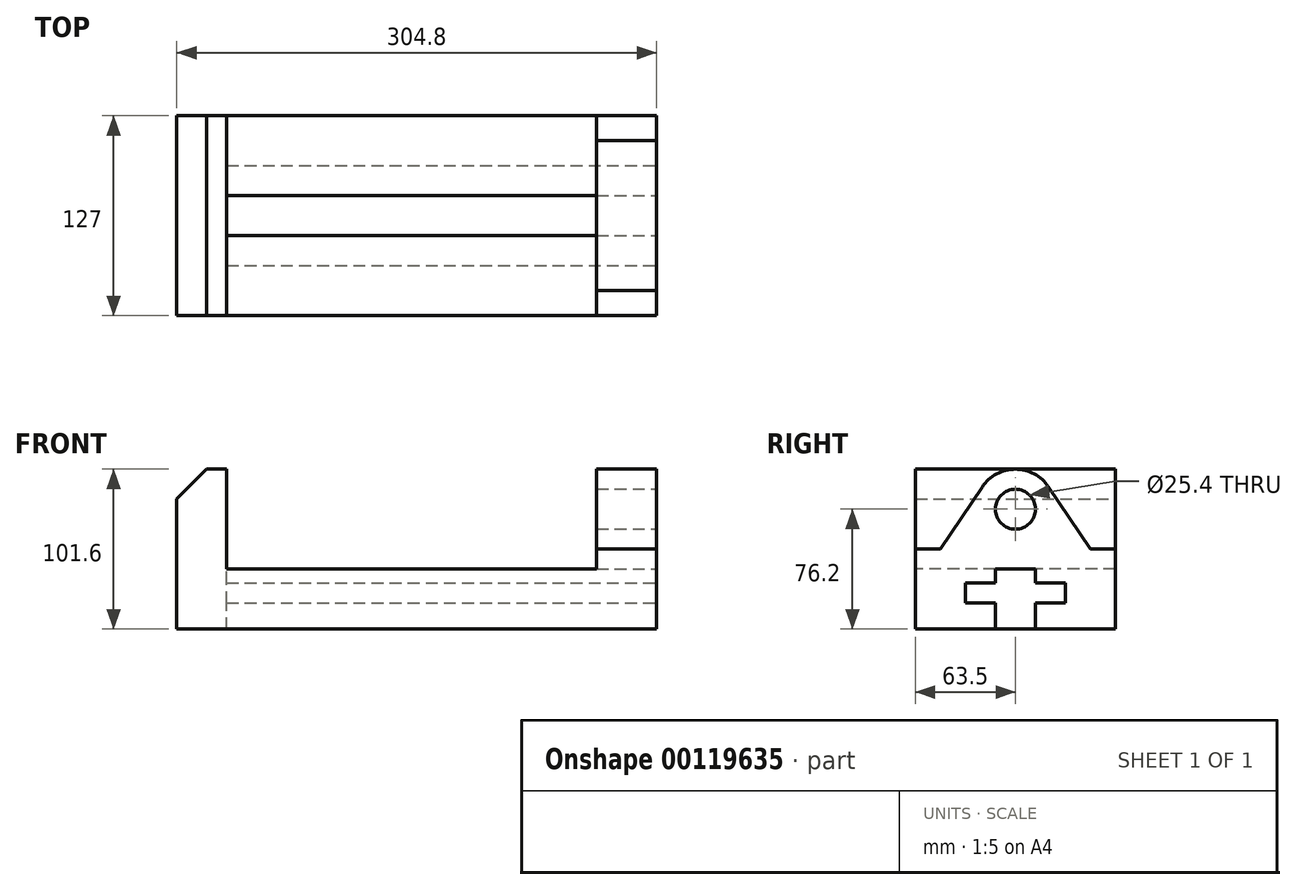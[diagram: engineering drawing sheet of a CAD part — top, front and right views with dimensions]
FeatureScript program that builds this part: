
annotation { "Feature Type Name" : "Feature", "Feature Type Description" : "" }
export const myFeature = defineFeature(function(context is Context, id is Id, definition is map)
    precondition{}
    {
        {
            var Q0;
            Q0=qCreatedBy(makeId("Front.planeOp"),FACE);
            var sketch = newSketch(context, id + "F0", { "sketchPlane" : qUnion([Q0])});
            skLineSegment(sketch, "E0", {"start": v(0, 0) * mm, "end": v(-304.8, 0) * mm});
            skLineSegment(sketch, "E1", {"start": v(-304.8, 0) * mm, "end": v(-304.8, 101.6) * mm});
            skLineSegment(sketch, "E2", {"start": v(-304.8, 101.6) * mm, "end": v(-273.05, 101.6) * mm});
            skLineSegment(sketch, "E3", {"start": v(-273.05, 101.6) * mm, "end": v(-273.05, 38.1) * mm});
            skLineSegment(sketch, "E4", {"start": v(-273.05, 38.1) * mm, "end": v(-38.1, 38.1) * mm});
            skLineSegment(sketch, "E5", {"start": v(-38.1, 38.1) * mm, "end": v(-38.1, 101.6) * mm});
            skLineSegment(sketch, "E6", {"start": v(-38.1, 101.6) * mm, "end": v(0, 101.6) * mm});
            skLineSegment(sketch, "E7", {"start": v(0, 101.6) * mm, "end": v(0, 0) * mm});
            skSolve(sketch);
        }
        {
            var Q0;
            Q0 = qSketchRegion(id + "F0", true);
            extrude(context, id + "F1", {"entities" : qUnion([Q0]), "oppositeDirection" : true, "depth" : 127 * mm});
        }
        {
            var Q0;
            Q0=makeQuery(id+"F1.opExtrude","SWEPT_EDGE",EDGE,{"disambiguationData":[OSD([sQuery(id+"F0.wireOp",EDGE,"E1"),sQuery(id+"F0.wireOp",EDGE,"E2")])]});
            chamfer(context, id + "F2", {"entities" : qUnion([Q0]), "width" : 19.05 * mm, "tangentPropagation" : true});
        }
        {
            var Q0;
            Q0=makeQuery(id+"F1.opExtrude","SWEPT_FACE",FACE,{"disambiguationData":[OSD([sQuery(id+"F0.wireOp",EDGE,"E7")])]});
            var sketch = newSketch(context, id + "F3", { "sketchPlane" : qUnion([Q0])});
            skLineSegment(sketch, "E8", {"start": v(63.5, 0) * mm, "end": v(50.8, 0) * mm});
            skLineSegment(sketch, "E9", {"start": v(50.8, 0) * mm, "end": v(50.8, 16.51) * mm});
            skLineSegment(sketch, "E10", {"start": v(50.8, 16.51) * mm, "end": v(31.75, 16.51) * mm});
            skLineSegment(sketch, "E11", {"start": v(31.75, 16.51) * mm, "end": v(31.75, 29.21) * mm});
            skLineSegment(sketch, "E12", {"start": v(31.75, 29.21) * mm, "end": v(50.8, 29.21) * mm});
            skLineSegment(sketch, "E13", {"start": v(50.8, 29.21) * mm, "end": v(50.8, 38.1) * mm});
            skLineSegment(sketch, "E14", {"start": v(50.8, 38.1) * mm, "end": v(76.2, 38.1) * mm});
            skLineSegment(sketch, "E15", {"start": v(76.2, 38.1) * mm, "end": v(76.2, 29.2) * mm});
            skLineSegment(sketch, "E16", {"start": v(76.2, 29.2) * mm, "end": v(95.25, 29.21) * mm});
            skLineSegment(sketch, "E17", {"start": v(95.25, 29.21) * mm, "end": v(95.25, 16.51) * mm});
            skLineSegment(sketch, "E18", {"start": v(95.25, 16.51) * mm, "end": v(76.2, 16.51) * mm});
            skLineSegment(sketch, "E19", {"start": v(76.2, 16.51) * mm, "end": v(76.2, 0) * mm});
            skLineSegment(sketch, "E20", {"start": v(76.2, 0) * mm, "end": v(63.5, 0) * mm});
            skSolve(sketch);
        }
        {
            var Q0;
            Q0 = qSketchRegion(id + "F3", true);
            extrude(context, id + "F4", {"entities" : qUnion([Q0]), "operationType" : NewBodyOperationType.REMOVE, "oppositeDirection" : true, "depth" : 273.05 * mm});
        }
        {
            var Q0;
            Q0=makeQuery(id+"F1.opExtrude","SWEPT_FACE",FACE,{"disambiguationData":[OSD([sQuery(id+"F0.wireOp",EDGE,"E7")])]});
            var sketch = newSketch(context, id + "F5", { "sketchPlane" : qUnion([Q0])});
            skLineSegment(sketch, "E21", {"start": v(63.5, 101.6) * mm, "end": v(0, 101.6) * mm});
            skLineSegment(sketch, "E22", {"start": v(0, 101.6) * mm, "end": v(0, 50.8) * mm});
            skLineSegment(sketch, "E23", {"start": v(0, 50.8) * mm, "end": v(15.88, 50.8) * mm});
            skLineSegment(sketch, "E24", {"start": v(63.5, 101.6) * mm, "end": v(127, 101.6) * mm});
            skLineSegment(sketch, "E25", {"start": v(127, 101.6) * mm, "end": v(127, 50.8) * mm});
            skLineSegment(sketch, "E26", {"start": v(127, 50.8) * mm, "end": v(111.13, 50.8) * mm});
            skPoint(sketch, "E27.visualSharp", {"position": v(63.5, 101.6) * mm});
            skArc(sketch, "E28", {"start": v(84.6, 90.35) * mm, "mid": v(63.5, 101.6) * mm, "end": v(42.4, 90.35) * mm});
            skLineSegment(sketch, "E29", {"start": v(42.4, 90.35) * mm, "end": v(15.88, 50.8) * mm});
            skLineSegment(sketch, "E30", {"start": v(84.6, 90.35) * mm, "end": v(111.13, 50.8) * mm});
            skCircle(sketch, "E31", {"center": v(63.5, 76.2) * mm, "radius": 12.7 * mm});
            skSolve(sketch);
        }
        {
            var Q0;
            Q0 = qSketchRegion(id + "F5", true);
            var Q1;
            Q1=makeQuery(id+"F1.opExtrude","SWEPT_FACE",FACE,{"disambiguationData":[OSD([sQuery(id+"F0.wireOp",EDGE,"E5")])]});
            extrude(context, id + "F6", {"entities" : qUnion([Q0]), "operationType" : NewBodyOperationType.REMOVE, "endBound" : BoundingType.UP_TO_SURFACE, "oppositeDirection" : true, "endBoundEntityFace" : qUnion([Q1]), "depth" : 25.4 * mm});
        }
    });
